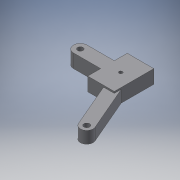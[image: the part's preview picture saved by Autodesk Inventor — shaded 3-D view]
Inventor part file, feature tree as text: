
AUTODESK INVENTOR PART (.ipt)
format: ipt  version: 2017 (Build 210142000, 142)  size: 160,256 bytes
history: native  units: mm
features: extrude x4, sketch x4, plane x1, projected_geometry x1
ambient origin geometry x8: Origin, YZ Plane, XZ Plane, XY Plane, X Axis, Y Axis, Z Axis, Center Point
bodies: Solid1 (feature_tree)
feature tree (10):
  extrude  "Extrusion1"  Depth=19.05mm
  extrude  "Extrusion2"  Depth=10.0mm
  extrude  "Extrusion3"  Depth=10.0mm
  sketch  "Sketch4"  dims[d6=40.0mm d7=15.0mm d8=0.0mm d9=5.0mm d10=0.0mm d11=5.0mm d12=10.0mm d13=0.0mm d14=80.0mm d15=40.0mm d16=8.5mm d17=10.0mm d18=10.0mm d19=5.0mm d20=10.0mm d21=0.0mm]
  plane  "Work Plane1"
  extrude  "Extrusion4"  Depth=15.0mm TaperAngle=0.0deg
  sketch  "Sketch1"  dims[d0=38.1mm d1=19.05mm]
  sketch  "Sketch2"  dims[d2=10.0mm d3=10.0mm]
  projected_geometry  "Projected Loop1"
  sketch  "Sketch3"  dims[d4=8.0mm d5=10.0mm]
